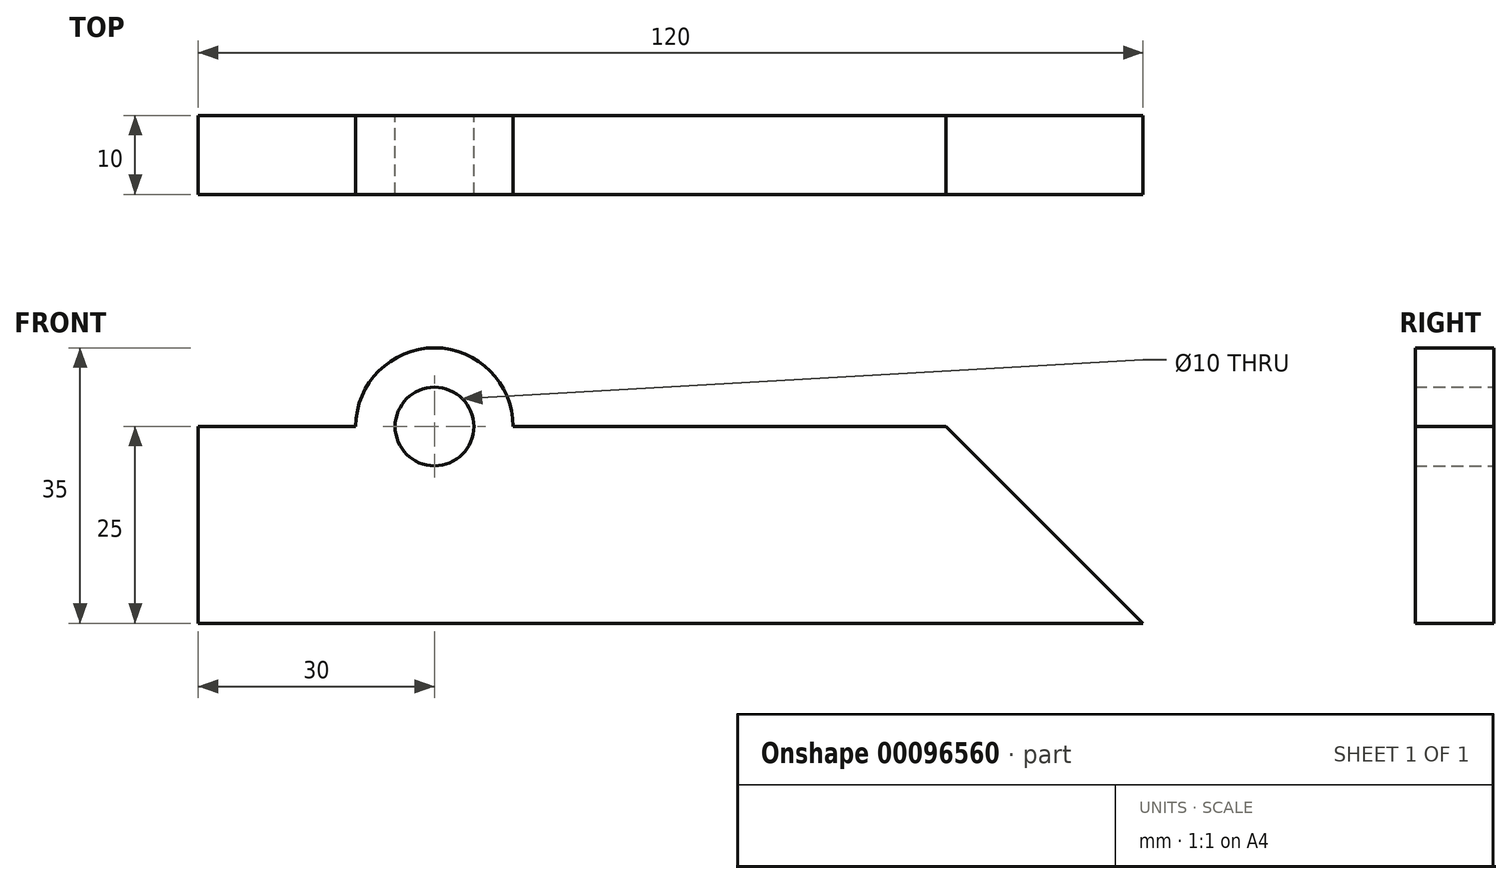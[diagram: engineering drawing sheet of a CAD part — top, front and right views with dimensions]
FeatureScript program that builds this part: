
annotation { "Feature Type Name" : "Feature", "Feature Type Description" : "" }
export const myFeature = defineFeature(function(context is Context, id is Id, definition is map)
    precondition{}
    {
        {
            var Q0;
            Q0=qCreatedBy(makeId("Front.planeOp"),FACE);
            var sketch = newSketch(context, id + "F0", { "sketchPlane" : qUnion([Q0])});
            skLineSegment(sketch, "E0", {"start": v(0, 0) * mm, "end": v(0, 25) * mm});
            skLineSegment(sketch, "E1", {"start": v(0, 25) * mm, "end": v(20, 25) * mm});
            skArc(sketch, "E2", {"start": v(40, 25) * mm, "mid": v(30, 35) * mm, "end": v(20, 25) * mm});
            skCircle(sketch, "E3", {"center": v(30, 25) * mm, "radius": 5 * mm});
            skLineSegment(sketch, "E4", {"start": v(40, 25) * mm, "end": v(95, 25) * mm});
            skLineSegment(sketch, "E5", {"start": v(95, 25) * mm, "end": v(120, 0) * mm});
            skLineSegment(sketch, "E6", {"start": v(120, 0) * mm, "end": v(0, 0) * mm});
            skSolve(sketch);
        }
        {
            var Q0;
            Q0 = qSketchRegion(id + "F0", true);
            extrude(context, id + "F1", {"entities" : qUnion([Q0]), "depth" : 10 * mm});
        }
    });
